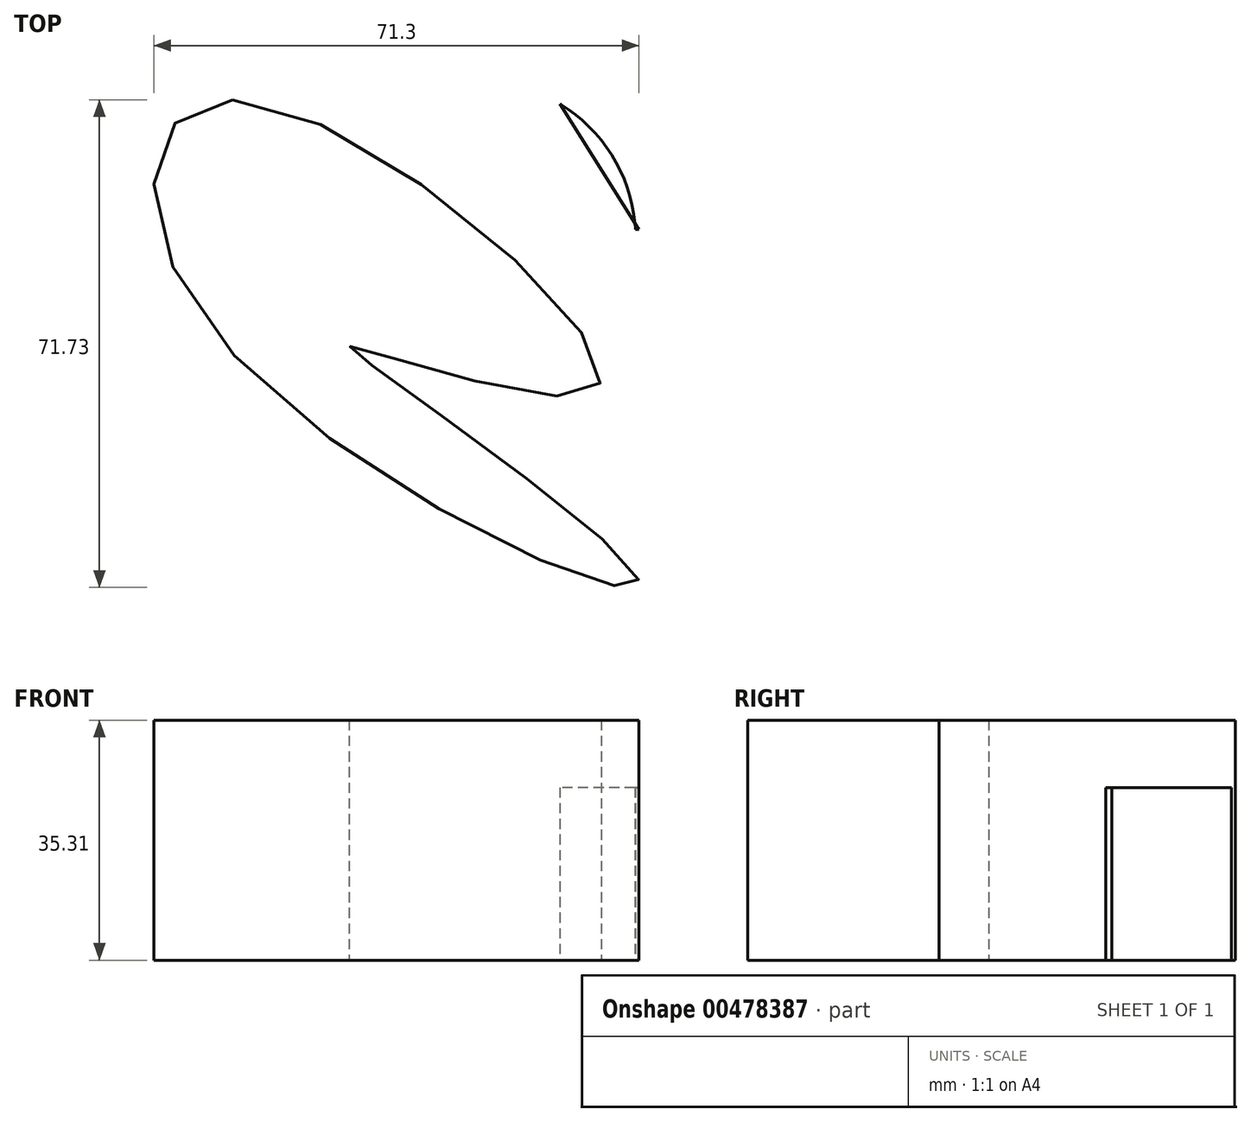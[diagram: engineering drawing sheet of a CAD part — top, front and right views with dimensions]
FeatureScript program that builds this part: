
annotation { "Feature Type Name" : "Feature", "Feature Type Description" : "" }
export const myFeature = defineFeature(function(context is Context, id is Id, definition is map)
    precondition{}
    {
        {
            var Q0;
            Q0=qCreatedBy(makeId("Top.planeOp"),FACE);
            var sketch = newSketch(context, id + "F0", { "sketchPlane" : qUnion([Q0])});
            skArc(sketch, "E0", {"start": v(-41.76, -15.7) * mm, "mid": v(-6.25, -16.68) * mm, "end": v(-11.58, 18.44) * mm});
            skLineSegment(sketch, "E1", {"start": v(-41.76, -15.7) * mm, "end": v(-23.6, -1.35) * mm});
            skLineSegment(sketch, "E2", {"start": v(-23.6, -1.35) * mm, "end": v(0, 0) * mm});
            skLineSegment(sketch, "E3", {"start": v(0, 0) * mm, "end": v(-11.58, 18.44) * mm});
            skSolve(sketch);
        }
        {
            var Q0;
            {var subQ0=sQuery(id+"F0.wireOp",EDGE,"E2");var subQ1=sQuery(id+"F0.wireOp",EDGE,"E0");var subQ2=makeQuery(id+"F0.imprint","INTERSECT",VERTEX,{"derivedFrom":[subQ1,subQ0]});Q0=makeQuery(id+"F0.imprint","IMPRINT",FACE,{"disambiguationData":[TD([[makeQuery(id+"F0.imprint","IMPRINT",EDGE,{"disambiguationData":[TD([[subQ2,-1.0]])],"derivedFrom":subQ1}),-1.0]])]});}
            var Q1;
            {var subQ0=sQuery(id+"F0.wireOp",EDGE,"E3");var subQ1=sQuery(id+"F0.wireOp",EDGE,"E0");var subQ2=makeQuery(id+"F0.imprint","INTERSECT",VERTEX,{"disambiguationData":[OD(0.0)],"derivedFrom":[subQ1,subQ0]});Q1=makeQuery(id+"F0.imprint","IMPRINT",FACE,{"disambiguationData":[TD([[makeQuery(id+"F0.imprint","IMPRINT",EDGE,{"disambiguationData":[TD([[subQ2,1.0]])],"derivedFrom":subQ1}),1.0]])]});}
            extrude(context, id + "F1", {"entities" : qUnion([Q0, Q1]), "depth" : 25.4 * mm});
        }
        {
            var Q0;
            Q0=makeQuery(id+"F1.opExtrude","CAP_FACE",FACE,{"disambiguationData":[OSD([sQuery(id+"F0.wireOp",EDGE,"E0"),sQuery(id+"F0.wireOp",EDGE,"E3")])],"isStart":false});
            extrude(context, id + "F2", {"entities" : qUnion([Q0]), "operationType" : NewBodyOperationType.ADD, "oppositeDirection" : true, "depth" : 7.37 * mm});
        }
        {
            var Q0;
            Q0=qCreatedBy(makeId("Top.planeOp"),FACE);
            var sketch = newSketch(context, id + "F3", { "sketchPlane" : qUnion([Q0])});
            skFitSpline(sketch, "E4", {"points": [v(-59.74, 19.05) * mm, v(-6.1, -23.32) * mm, v(-42.37, -17.22) * mm, v(-42.06, -17.83) * mm, v(0, -51.66) * mm, v(-64.62, -12.34) * mm, v(-59.74, 19.05) * mm]});
            skSolve(sketch);
        }
        {
            var Q0;
            Q0=makeQuery(id+"F3.imprint","IMPRINT",FACE,{"disambiguationData":[TD([[makeQuery(id+"F3.imprint","IMPRINT",EDGE,{"derivedFrom":sQuery(id+"F3.wireOp",EDGE,"E4")}),-1.0]])]});
            extrude(context, id + "F4", {"entities" : qUnion([Q0]), "depth" : 35.3 * mm});
        }
    });
